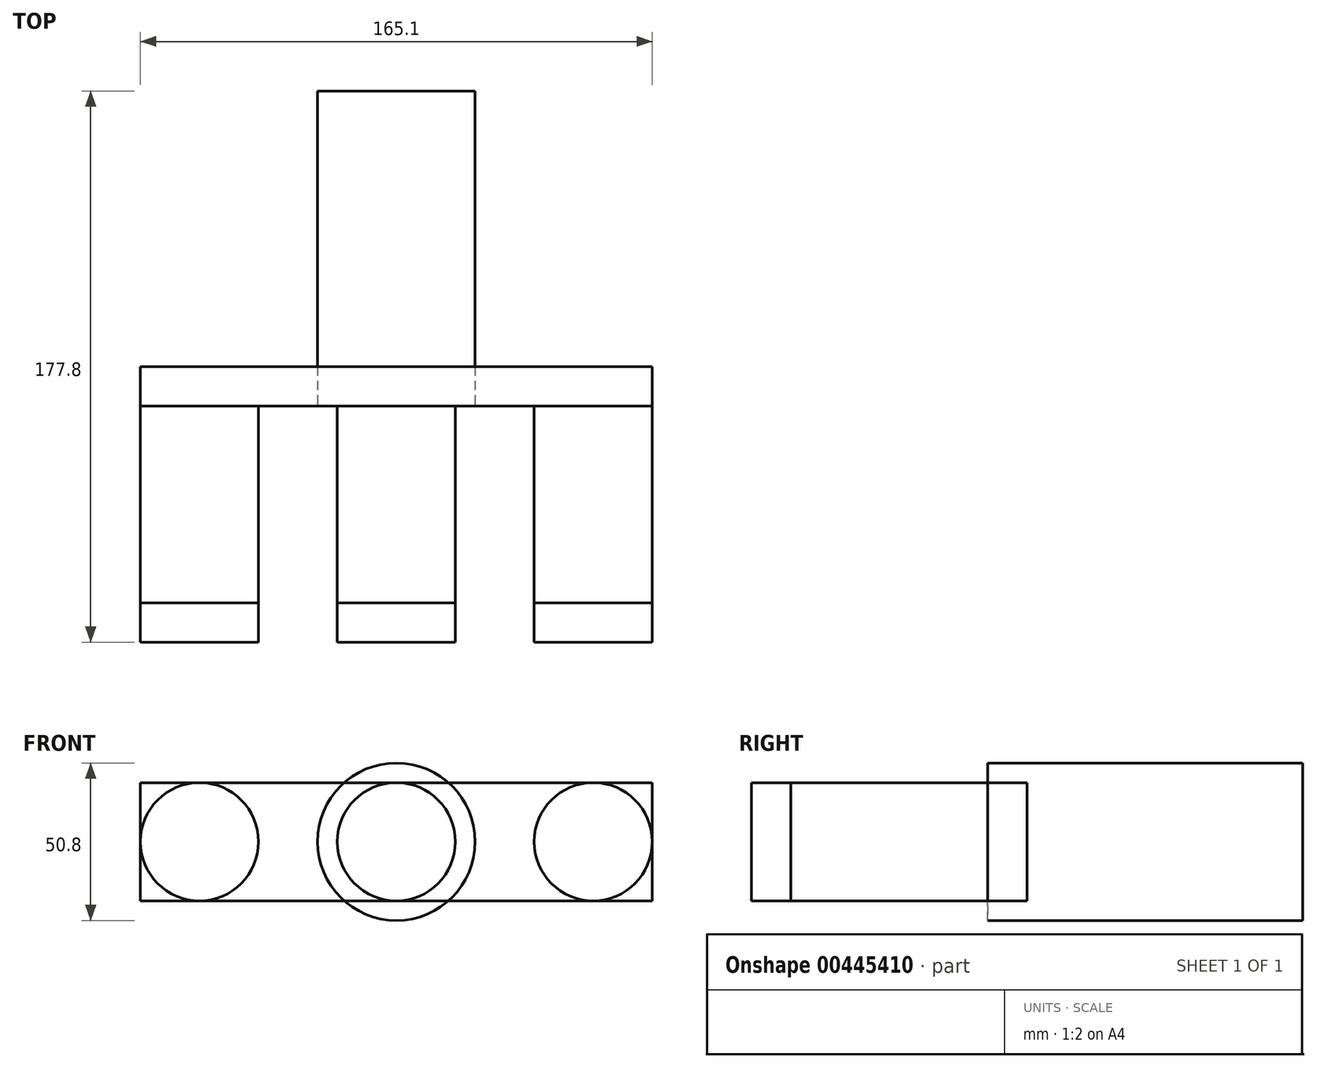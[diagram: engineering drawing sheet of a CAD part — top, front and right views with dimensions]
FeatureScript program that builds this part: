
annotation { "Feature Type Name" : "Feature", "Feature Type Description" : "" }
export const myFeature = defineFeature(function(context is Context, id is Id, definition is map)
    precondition{}
    {
        {
            var Q0;
            Q0=qCreatedBy(makeId("Front.planeOp"),FACE);
            var sketch = newSketch(context, id + "F0", { "sketchPlane" : qUnion([Q0])});
            skCircle(sketch, "E0", {"center": v(0, 0) * mm, "radius": 19.05 * mm});
            skLineSegment(sketch, "E1", {"start": v(0, 0) * mm, "end": v(-63.5, 0) * mm});
            skCircle(sketch, "E2", {"center": v(-63.5, 0) * mm, "radius": 19.05 * mm});
            skLineSegment(sketch, "E3", {"start": v(0, 0) * mm, "end": v(63.5, 0) * mm});
            skCircle(sketch, "E4", {"center": v(63.5, 0) * mm, "radius": 19.05 * mm});
            skSolve(sketch);
        }
        {
            var Q0;
            Q0=makeQuery(id+"F0.imprint","IMPRINT",FACE,{"disambiguationData":[TD([[makeQuery(id+"F0.imprint","IMPRINT",EDGE,{"derivedFrom":sQuery(id+"F0.wireOp",EDGE,"E4")}),1.0]])]});
            var Q1;
            {var subQ0=sQuery(id+"F0.wireOp",EDGE,"E1");var subQ1=sQuery(id+"F0.wireOp",EDGE,"E0");var subQ2=makeQuery(id+"F0.imprint","INTERSECT",VERTEX,{"derivedFrom":[subQ1,subQ0]});Q1=makeQuery(id+"F0.imprint","IMPRINT",FACE,{"disambiguationData":[TD([[makeQuery(id+"F0.imprint","IMPRINT",EDGE,{"disambiguationData":[TD([[subQ2,-1.0]])],"derivedFrom":subQ1}),1.0]])]});}
            var Q2;
            Q2=makeQuery(id+"F0.imprint","IMPRINT",FACE,{"disambiguationData":[TD([[makeQuery(id+"F0.imprint","IMPRINT",EDGE,{"derivedFrom":sQuery(id+"F0.wireOp",EDGE,"E2")}),1.0]])]});
            var Q3;
            {var subQ0=sQuery(id+"F0.wireOp",EDGE,"E1");var subQ1=sQuery(id+"F0.wireOp",EDGE,"E0");var subQ2=makeQuery(id+"F0.imprint","INTERSECT",VERTEX,{"derivedFrom":[subQ1,subQ0]});Q3=makeQuery(id+"F0.imprint","IMPRINT",FACE,{"disambiguationData":[TD([[makeQuery(id+"F0.imprint","IMPRINT",EDGE,{"disambiguationData":[TD([[subQ2,1.0]])],"derivedFrom":subQ1}),1.0]])]});}
            extrude(context, id + "F1", {"entities" : qUnion([Q0, Q1, Q2, Q3]), "depth" : 76.2 * mm});
        }
        {
            var Q0;
            Q0=qCreatedBy(makeId("Front.planeOp"),FACE);
            var sketch = newSketch(context, id + "F2", { "sketchPlane" : qUnion([Q0])});
            skLineSegment(sketch, "E5.bottom", {"start": v(-82.55, 19.05) * mm, "end": v(82.55, 19.05) * mm});
            skLineSegment(sketch, "E5.top", {"start": v(-82.55, -19.05) * mm, "end": v(82.55, -19.05) * mm});
            skLineSegment(sketch, "E5.left", {"start": v(-82.55, 19.05) * mm, "end": v(-82.55, -19.05) * mm});
            skLineSegment(sketch, "E5.right", {"start": v(82.55, 19.05) * mm, "end": v(82.55, -19.05) * mm});
            skPoint(sketch, "E5.middle", {"position": v(0, 0) * mm});
            skSolve(sketch);
        }
        {
            var Q0;
            Q0=makeQuery(id+"F1.opExtrude","CAP_FACE",FACE,{"disambiguationData":[OSD([sQuery(id+"F0.wireOp",EDGE,"E2")])],"isStart":false});
            var Q1;
            Q1=makeQuery(id+"F1.opExtrude","CAP_FACE",FACE,{"disambiguationData":[OSD([sQuery(id+"F0.wireOp",EDGE,"E0")])],"isStart":false});
            var Q2;
            Q2=makeQuery(id+"F1.opExtrude","CAP_FACE",FACE,{"disambiguationData":[OSD([sQuery(id+"F0.wireOp",EDGE,"E4")])],"isStart":false});
            var Q3;
            Q3=makeQuery(id+"F2.imprint","IMPRINT",FACE,{"disambiguationData":[TD([[makeQuery(id+"F2.imprint","IMPRINT",EDGE,{"derivedFrom":sQuery(id+"F2.wireOp",EDGE,"E5.bottom")}),-1.0]])]});
            extrude(context, id + "F3", {"entities" : qUnion([Q0, Q1, Q2, Q3]), "oppositeDirection" : true, "depth" : 12.7 * mm});
        }
        {
            var Q0;
            Q0=qCreatedBy(makeId("Front.planeOp"),FACE);
            var sketch = newSketch(context, id + "F4", { "sketchPlane" : qUnion([Q0])});
            skCircle(sketch, "E6", {"center": v(0, 0) * mm, "radius": 25.4 * mm});
            skSolve(sketch);
        }
        {
            var Q0;
            Q0 = qSketchRegion(id + "F4", true);
            extrude(context, id + "F5", {"entities" : qUnion([Q0]), "oppositeDirection" : true, "depth" : 101.6 * mm});
        }
    });
